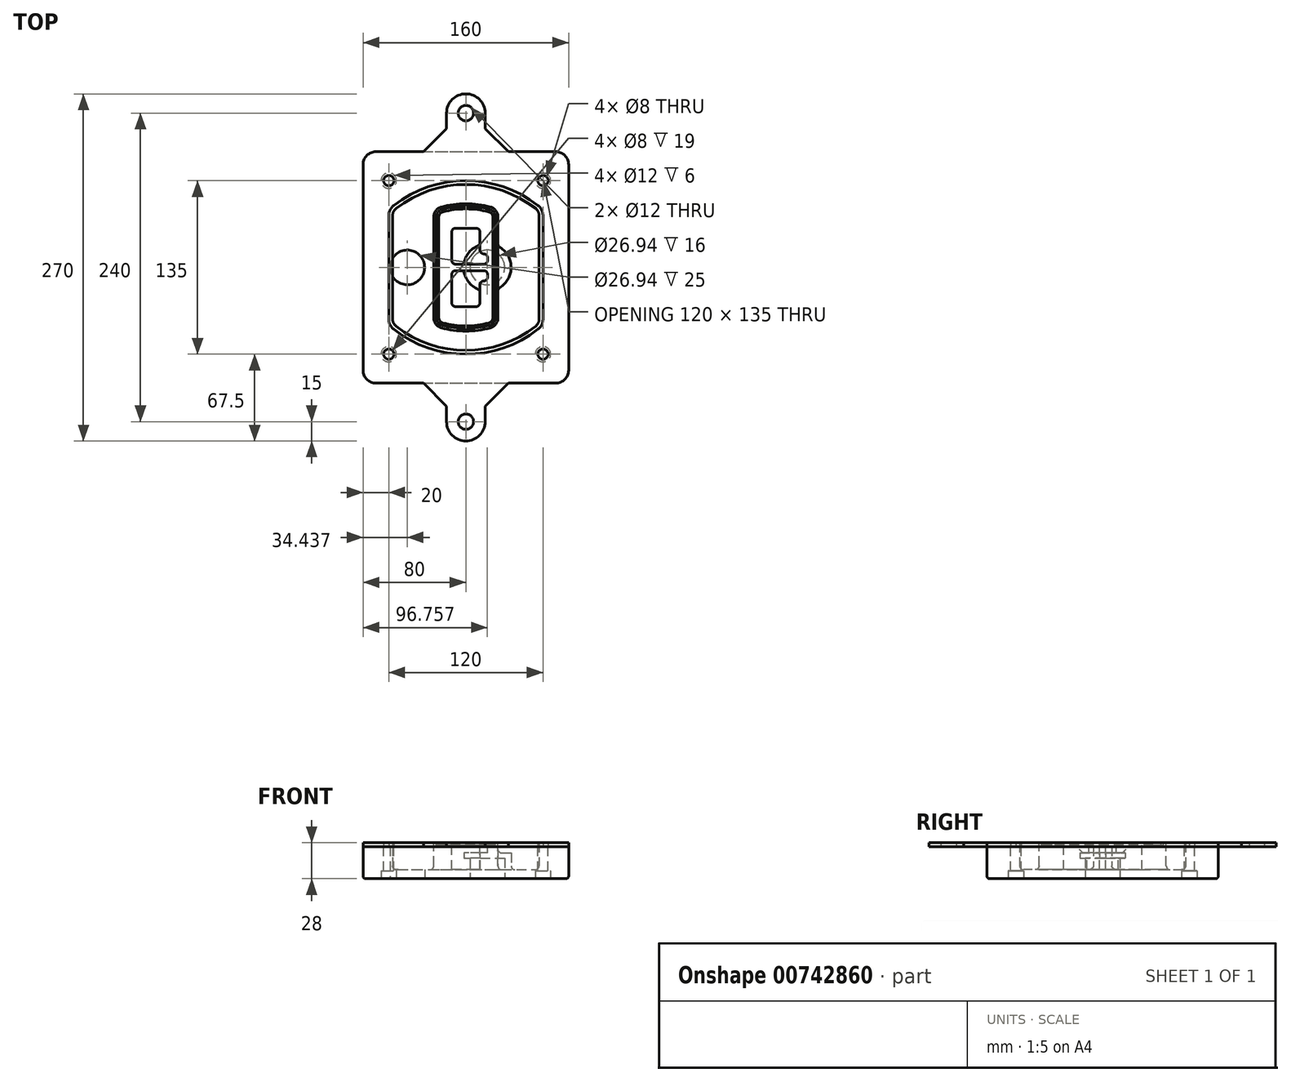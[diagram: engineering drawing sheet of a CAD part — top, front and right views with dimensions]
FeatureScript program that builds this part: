
annotation { "Feature Type Name" : "Feature", "Feature Type Description" : "" }
export const myFeature = defineFeature(function(context is Context, id is Id, definition is map)
    precondition{}
    {
        {
            var Q0;
            Q0=qCreatedBy(makeId("Top.planeOp"),FACE);
            var sketch = newSketch(context, id + "F0", { "sketchPlane" : qUnion([Q0])});
            skPoint(sketch, "E0.rect.middle", {"position": v(0, 0) * mm});
            skLineSegment(sketch, "E1.bottom", {"start": v(-70, -90) * mm, "end": v(70, -90) * mm});
            skLineSegment(sketch, "E1.top", {"start": v(-70, 90) * mm, "end": v(70, 90) * mm});
            skLineSegment(sketch, "E1.left", {"start": v(-80, -80) * mm, "end": v(-80, 80) * mm});
            skLineSegment(sketch, "E1.right", {"start": v(80, -80) * mm, "end": v(80, 80) * mm});
            skLineSegment(sketch, "E2", {"start": v(-80, 90) * mm, "end": v(80, -90) * mm, "construction": true});
            skLineSegment(sketch, "E3", {"start": v(80, 90) * mm, "end": v(-80, -90) * mm, "construction": true});
            skCircle(sketch, "E4", {"center": v(-60, 67.5) * mm, "radius": 4 * mm});
            skCircle(sketch, "E5", {"center": v(60, 67.5) * mm, "radius": 4 * mm});
            skCircle(sketch, "E6", {"center": v(60, -67.5) * mm, "radius": 4 * mm});
            skCircle(sketch, "E7", {"center": v(-60, -67.5) * mm, "radius": 4 * mm});
            skLineSegment(sketch, "E8", {"start": v(-60, 67.5) * mm, "end": v(60, 67.5) * mm, "construction": true});
            skLineSegment(sketch, "E9", {"start": v(60, 67.5) * mm, "end": v(60, -67.5) * mm, "construction": true});
            skLineSegment(sketch, "E10", {"start": v(60, -67.5) * mm, "end": v(-60, -67.5) * mm, "construction": true});
            skLineSegment(sketch, "E11", {"start": v(-60, -67.5) * mm, "end": v(-60, 67.5) * mm, "construction": true});
            skLineSegment(sketch, "E12", {"start": v(-60, 40.3) * mm, "end": v(-60, -40.3) * mm});
            skLineSegment(sketch, "E13", {"start": v(60, 40.3) * mm, "end": v(60, -40.3) * mm});
            skArc(sketch, "E14", {"start": v(56.15, 48.18) * mm, "mid": v(0, 67.5) * mm, "end": v(-56.15, 48.18) * mm});
            skArc(sketch, "E15", {"start": v(-56.15, -48.18) * mm, "mid": v(0, -67.5) * mm, "end": v(56.15, -48.18) * mm});
            skLineSegment(sketch, "E16", {"start": v(-60, 0) * mm, "end": v(60, 0) * mm, "construction": true});
            skPoint(sketch, "E17.visualSharp", {"position": v(-60, -45) * mm});
            skArc(sketch, "E17.filletArc", {"start": v(-60, -40.3) * mm, "mid": v(-58.99, -44.68) * mm, "end": v(-56.15, -48.18) * mm});
            skPoint(sketch, "E18.visualSharp", {"position": v(-60, 45) * mm});
            skArc(sketch, "E18.filletArc", {"start": v(-56.15, 48.18) * mm, "mid": v(-58.99, 44.68) * mm, "end": v(-60, 40.3) * mm});
            skPoint(sketch, "E19.visualSharp", {"position": v(60, 45) * mm});
            skArc(sketch, "E19.filletArc", {"start": v(60, 40.3) * mm, "mid": v(58.99, 44.68) * mm, "end": v(56.15, 48.18) * mm});
            skPoint(sketch, "E20.visualSharp", {"position": v(60, -45) * mm});
            skArc(sketch, "E20.filletArc", {"start": v(56.15, -48.18) * mm, "mid": v(58.99, -44.68) * mm, "end": v(60, -40.3) * mm});
            skPoint(sketch, "E21.visualSharp", {"position": v(-80, 90) * mm});
            skArc(sketch, "E21.filletArc", {"start": v(-70, 90) * mm, "mid": v(-77.07, 87.07) * mm, "end": v(-80, 80) * mm});
            skPoint(sketch, "E22.visualSharp", {"position": v(80, 90) * mm});
            skArc(sketch, "E22.filletArc", {"start": v(80, 80) * mm, "mid": v(77.07, 87.07) * mm, "end": v(70, 90) * mm});
            skPoint(sketch, "E23.visualSharp", {"position": v(80, -90) * mm});
            skArc(sketch, "E23.filletArc", {"start": v(70, -90) * mm, "mid": v(77.07, -87.07) * mm, "end": v(80, -80) * mm});
            skPoint(sketch, "E24.visualSharp", {"position": v(-80, -90) * mm});
            skArc(sketch, "E24.filletArc", {"start": v(-80, -80) * mm, "mid": v(-77.07, -87.07) * mm, "end": v(-70, -90) * mm});
            skArc(sketch, "E25.0", {"start": v(57, 40.3) * mm, "mid": v(56.3, 43.36) * mm, "end": v(54.3, 45.81) * mm});
            skLineSegment(sketch, "E25.1", {"start": v(57, 40.3) * mm, "end": v(57, -40.3) * mm});
            skArc(sketch, "E25.2", {"start": v(54.3, -45.81) * mm, "mid": v(56.3, -43.36) * mm, "end": v(57, -40.3) * mm});
            skArc(sketch, "E25.3", {"start": v(-54.3, -45.81) * mm, "mid": v(0, -64.5) * mm, "end": v(54.3, -45.81) * mm});
            skArc(sketch, "E25.4", {"start": v(-57, -40.3) * mm, "mid": v(-56.3, -43.36) * mm, "end": v(-54.3, -45.81) * mm});
            skArc(sketch, "E25.5", {"start": v(54.3, 45.81) * mm, "mid": v(0, 64.5) * mm, "end": v(-54.3, 45.81) * mm});
            skLineSegment(sketch, "E25.6", {"start": v(-57, 40.3) * mm, "end": v(-57, -40.3) * mm});
            skArc(sketch, "E25.7", {"start": v(-54.3, 45.81) * mm, "mid": v(-56.3, 43.36) * mm, "end": v(-57, 40.3) * mm});
            skArc(sketch, "E26.0", {"start": v(-58.62, 51.33) * mm, "mid": v(-62.58, 46.43) * mm, "end": v(-64, 40.3) * mm});
            skArc(sketch, "E26.1", {"start": v(58.62, 51.33) * mm, "mid": v(0, 71.5) * mm, "end": v(-58.62, 51.33) * mm});
            skArc(sketch, "E26.2", {"start": v(64, 40.3) * mm, "mid": v(62.58, 46.43) * mm, "end": v(58.62, 51.33) * mm});
            skLineSegment(sketch, "E26.3", {"start": v(64, 40.3) * mm, "end": v(64, -40.3) * mm});
            skArc(sketch, "E26.4", {"start": v(58.62, -51.33) * mm, "mid": v(62.58, -46.43) * mm, "end": v(64, -40.3) * mm});
            skLineSegment(sketch, "E26.5", {"start": v(-64, 40.3) * mm, "end": v(-64, -40.3) * mm});
            skArc(sketch, "E26.6", {"start": v(-58.62, -51.33) * mm, "mid": v(0, -71.5) * mm, "end": v(58.62, -51.33) * mm});
            skArc(sketch, "E26.7", {"start": v(-64, -40.3) * mm, "mid": v(-62.58, -46.43) * mm, "end": v(-58.62, -51.33) * mm});
            skSolve(sketch);
        }
        {
            var Q0;
            Q0=makeQuery(id+"F0.imprint","IMPRINT",FACE,{"disambiguationData":[TD([[makeQuery(id+"F0.imprint","IMPRINT",EDGE,{"derivedFrom":sQuery(id+"F0.wireOp",EDGE,"E1.bottom")}),1.0]])]});
            var Q1;
            Q1=makeQuery(id+"F0.imprint","IMPRINT",FACE,{"disambiguationData":[TD([[makeQuery(id+"F0.imprint","IMPRINT",EDGE,{"derivedFrom":sQuery(id+"F0.wireOp",EDGE,"E12")}),1.0]])]});
            var Q2;
            Q2=makeQuery(id+"F0.imprint","IMPRINT",FACE,{"disambiguationData":[TD([[makeQuery(id+"F0.imprint","IMPRINT",EDGE,{"derivedFrom":sQuery(id+"F0.wireOp",EDGE,"E25.0")}),1.0]])]});
            var Q3;
            Q3=makeQuery(id+"F0.imprint","IMPRINT",FACE,{"disambiguationData":[TD([[makeQuery(id+"F0.imprint","IMPRINT",EDGE,{"derivedFrom":sQuery(id+"F0.wireOp",EDGE,"E12")}),-1.0]])]});
            extrude(context, id + "F1", {"entities" : qUnion([Q0, Q1, Q2, Q3]), "oppositeDirection" : true, "depth" : 25 * mm});
        }
        {
            var Q0;
            Q0=makeQuery(id+"F0.imprint","IMPRINT",FACE,{"disambiguationData":[TD([[makeQuery(id+"F0.imprint","IMPRINT",EDGE,{"derivedFrom":sQuery(id+"F0.wireOp",EDGE,"E12")}),1.0]])]});
            extrude(context, id + "F2", {"entities" : qUnion([Q0]), "operationType" : NewBodyOperationType.ADD, "depth" : 3 * mm});
        }
        {
            var Q0;
            Q0=makeQuery(id+"F0.imprint","IMPRINT",FACE,{"disambiguationData":[TD([[makeQuery(id+"F0.imprint","IMPRINT",EDGE,{"derivedFrom":sQuery(id+"F0.wireOp",EDGE,"E25.0")}),1.0]])]});
            extrude(context, id + "F3", {"entities" : qUnion([Q0]), "operationType" : NewBodyOperationType.REMOVE, "oppositeDirection" : true, "depth" : 18 * mm});
        }
        {
            var Q0;
            Q0=makeQuery(id+"F2.opExtrude","CAP_FACE",FACE,{"disambiguationData":[OSD([sQuery(id+"F0.wireOp",EDGE,"E12"),sQuery(id+"F0.wireOp",EDGE,"E13"),sQuery(id+"F0.wireOp",EDGE,"E14"),sQuery(id+"F0.wireOp",EDGE,"E15"),sQuery(id+"F0.wireOp",EDGE,"E17.filletArc"),sQuery(id+"F0.wireOp",EDGE,"E18.filletArc"),sQuery(id+"F0.wireOp",EDGE,"E19.filletArc"),sQuery(id+"F0.wireOp",EDGE,"E20.filletArc"),sQuery(id+"F0.wireOp",EDGE,"E25.0"),sQuery(id+"F0.wireOp",EDGE,"E25.1"),sQuery(id+"F0.wireOp",EDGE,"E25.2"),sQuery(id+"F0.wireOp",EDGE,"E25.3"),sQuery(id+"F0.wireOp",EDGE,"E25.4"),sQuery(id+"F0.wireOp",EDGE,"E25.5"),sQuery(id+"F0.wireOp",EDGE,"E25.6"),sQuery(id+"F0.wireOp",EDGE,"E25.7")])],"isStart":false});
            var sketch = newSketch(context, id + "F4", { "sketchPlane" : qUnion([Q0])});
            skArc(sketch, "E27.0", {"start": v(-19.08, -46.97) * mm, "mid": v(0, -49.5) * mm, "end": v(19.08, -46.97) * mm});
            skArc(sketch, "E28.0", {"start": v(19.08, 46.97) * mm, "mid": v(0, 49.5) * mm, "end": v(-19.08, 46.97) * mm});
            skLineSegment(sketch, "E29", {"start": v(-25, 39.25) * mm, "end": v(-25, -39.25) * mm});
            skLineSegment(sketch, "E30", {"start": v(25, 39.25) * mm, "end": v(25, -39.25) * mm});
            skLineSegment(sketch, "E31", {"start": v(-25, 45.1) * mm, "end": v(25, 45.1) * mm, "construction": true});
            skLineSegment(sketch, "E32", {"start": v(-25, -45.1) * mm, "end": v(25, -45.1) * mm, "construction": true});
            skPoint(sketch, "E33.visualSharp", {"position": v(-25, 45.1) * mm});
            skArc(sketch, "E33.filletArc", {"start": v(-19.08, 46.97) * mm, "mid": v(-23.35, 44.11) * mm, "end": v(-25, 39.25) * mm});
            skPoint(sketch, "E34.visualSharp", {"position": v(25, 45.1) * mm});
            skArc(sketch, "E34.filletArc", {"start": v(25, 39.25) * mm, "mid": v(23.35, 44.11) * mm, "end": v(19.08, 46.97) * mm});
            skPoint(sketch, "E35.visualSharp", {"position": v(25, -45.1) * mm});
            skArc(sketch, "E35.filletArc", {"start": v(19.08, -46.97) * mm, "mid": v(23.35, -44.11) * mm, "end": v(25, -39.25) * mm});
            skPoint(sketch, "E36.visualSharp", {"position": v(-25, -45.1) * mm});
            skArc(sketch, "E36.filletArc", {"start": v(-25, -39.25) * mm, "mid": v(-23.35, -44.11) * mm, "end": v(-19.08, -46.97) * mm});
            skArc(sketch, "E37.0", {"start": v(54.3, 45.81) * mm, "mid": v(0, 64.5) * mm, "end": v(-54.3, 45.81) * mm});
            skArc(sketch, "E37.1", {"start": v(-54.3, 45.81) * mm, "mid": v(-56.3, 43.36) * mm, "end": v(-57, 40.3) * mm});
            skLineSegment(sketch, "E37.2", {"start": v(-57, 40.3) * mm, "end": v(-57, -40.3) * mm});
            skArc(sketch, "E37.3", {"start": v(-57, -40.3) * mm, "mid": v(-56.3, -43.36) * mm, "end": v(-54.3, -45.81) * mm});
            skArc(sketch, "E37.4", {"start": v(-54.3, -45.81) * mm, "mid": v(0, -64.5) * mm, "end": v(54.3, -45.81) * mm});
            skArc(sketch, "E37.5", {"start": v(54.3, -45.81) * mm, "mid": v(56.3, -43.36) * mm, "end": v(57, -40.3) * mm});
            skLineSegment(sketch, "E37.6", {"start": v(57, 40.3) * mm, "end": v(57, -40.3) * mm});
            skArc(sketch, "E37.7", {"start": v(57, 40.3) * mm, "mid": v(56.3, 43.36) * mm, "end": v(54.3, 45.81) * mm});
            skLineSegment(sketch, "E38.0", {"start": v(23, 39.25) * mm, "end": v(23, -39.25) * mm});
            skArc(sketch, "E38.1", {"start": v(18.56, -45.04) * mm, "mid": v(21.76, -42.9) * mm, "end": v(23, -39.25) * mm});
            skArc(sketch, "E38.2", {"start": v(-18.56, -45.04) * mm, "mid": v(0, -47.5) * mm, "end": v(18.56, -45.04) * mm});
            skArc(sketch, "E38.3", {"start": v(-23, -39.25) * mm, "mid": v(-21.76, -42.9) * mm, "end": v(-18.56, -45.04) * mm});
            skLineSegment(sketch, "E38.4", {"start": v(-23, 39.25) * mm, "end": v(-23, -39.25) * mm});
            skArc(sketch, "E38.5", {"start": v(23, 39.25) * mm, "mid": v(21.76, 42.9) * mm, "end": v(18.56, 45.04) * mm});
            skArc(sketch, "E38.6", {"start": v(-18.56, 45.04) * mm, "mid": v(-21.76, 42.9) * mm, "end": v(-23, 39.25) * mm});
            skArc(sketch, "E38.7", {"start": v(18.56, 45.04) * mm, "mid": v(0, 47.5) * mm, "end": v(-18.56, 45.04) * mm});
            skArc(sketch, "E39.0", {"start": v(21, 39.25) * mm, "mid": v(20.18, 41.68) * mm, "end": v(18.04, 43.1) * mm});
            skLineSegment(sketch, "E39.1", {"start": v(21, 39.25) * mm, "end": v(21, -39.25) * mm});
            skArc(sketch, "E39.2", {"start": v(18.04, -43.1) * mm, "mid": v(20.18, -41.68) * mm, "end": v(21, -39.25) * mm});
            skArc(sketch, "E39.3", {"start": v(-18.04, -43.1) * mm, "mid": v(0, -45.5) * mm, "end": v(18.04, -43.1) * mm});
            skArc(sketch, "E39.4", {"start": v(-21, -39.25) * mm, "mid": v(-20.18, -41.68) * mm, "end": v(-18.04, -43.1) * mm});
            skArc(sketch, "E39.5", {"start": v(18.04, 43.1) * mm, "mid": v(0, 45.5) * mm, "end": v(-18.04, 43.1) * mm});
            skLineSegment(sketch, "E39.6", {"start": v(-21, 39.25) * mm, "end": v(-21, -39.25) * mm});
            skArc(sketch, "E39.7", {"start": v(-18.04, 43.1) * mm, "mid": v(-20.18, 41.68) * mm, "end": v(-21, 39.25) * mm});
            skLineSegment(sketch, "E40", {"start": v(-25, 0) * mm, "end": v(25, 0) * mm, "construction": true});
            skLineSegment(sketch, "E41", {"start": v(-11, 5.5) * mm, "end": v(-11, 27.5) * mm});
            skLineSegment(sketch, "E42", {"start": v(-8, 30.5) * mm, "end": v(8, 30.5) * mm});
            skLineSegment(sketch, "E43", {"start": v(11, 27.5) * mm, "end": v(11, 13.5) * mm});
            skLineSegment(sketch, "E44", {"start": v(14, 10.5) * mm, "end": v(14, 10.5) * mm});
            skLineSegment(sketch, "E45", {"start": v(17, 7.5) * mm, "end": v(17, 5.5) * mm});
            skLineSegment(sketch, "E46", {"start": v(14, 2.5) * mm, "end": v(-8, 2.5) * mm});
            skPoint(sketch, "E47.visualSharp", {"position": v(-11, 30.5) * mm});
            skArc(sketch, "E47.filletArc", {"start": v(-8, 30.5) * mm, "mid": v(-10.12, 29.62) * mm, "end": v(-11, 27.5) * mm});
            skPoint(sketch, "E48.visualSharp", {"position": v(11, 30.5) * mm});
            skArc(sketch, "E48.filletArc", {"start": v(11, 27.5) * mm, "mid": v(10.12, 29.62) * mm, "end": v(8, 30.5) * mm});
            skPoint(sketch, "E49.visualSharp", {"position": v(11, 10.5) * mm});
            skArc(sketch, "E49.filletArc", {"start": v(11, 13.5) * mm, "mid": v(11.88, 11.38) * mm, "end": v(14, 10.5) * mm});
            skPoint(sketch, "E50.visualSharp", {"position": v(17, 10.5) * mm});
            skArc(sketch, "E50.filletArc", {"start": v(17, 7.5) * mm, "mid": v(16.12, 9.62) * mm, "end": v(14, 10.5) * mm});
            skPoint(sketch, "E51.visualSharp", {"position": v(17, 2.5) * mm});
            skArc(sketch, "E51.filletArc", {"start": v(14, 2.5) * mm, "mid": v(16.12, 3.38) * mm, "end": v(17, 5.5) * mm});
            skPoint(sketch, "E52.visualSharp", {"position": v(-11, 2.5) * mm});
            skArc(sketch, "E52.filletArc", {"start": v(-11, 5.5) * mm, "mid": v(-10.12, 3.38) * mm, "end": v(-8, 2.5) * mm});
            skLineSegment(sketch, "E53.0.MirrorCS", {"start": v(14, -2.5) * mm, "end": v(-8, -2.5) * mm});
            skArc(sketch, "E54.0.MirrorCS", {"start": v(-11, -5.5) * mm, "mid": v(-10.12, -3.38) * mm, "end": v(-8, -2.5) * mm});
            skLineSegment(sketch, "E55.0.MirrorCS", {"start": v(-11, -5.5) * mm, "end": v(-11, -27.5) * mm});
            skArc(sketch, "E56.0.MirrorCS", {"start": v(-8, -30.5) * mm, "mid": v(-10.12, -29.62) * mm, "end": v(-11, -27.5) * mm});
            skLineSegment(sketch, "E57.0.MirrorCS", {"start": v(-8, -30.5) * mm, "end": v(8, -30.5) * mm});
            skArc(sketch, "E58.0.MirrorCS", {"start": v(11, -27.5) * mm, "mid": v(10.12, -29.62) * mm, "end": v(8, -30.5) * mm});
            skLineSegment(sketch, "E59.0.MirrorCS", {"start": v(11, -27.5) * mm, "end": v(11, -13.5) * mm});
            skArc(sketch, "E60.0.MirrorCS", {"start": v(11, -13.5) * mm, "mid": v(11.88, -11.38) * mm, "end": v(14, -10.5) * mm});
            skArc(sketch, "E61.0.MirrorCS", {"start": v(17, -7.5) * mm, "mid": v(16.12, -9.62) * mm, "end": v(14, -10.5) * mm});
            skLineSegment(sketch, "E62.0.MirrorCS", {"start": v(17, -7.5) * mm, "end": v(17, -5.5) * mm});
            skArc(sketch, "E63.0.MirrorCS", {"start": v(14, -2.5) * mm, "mid": v(16.12, -3.38) * mm, "end": v(17, -5.5) * mm});
            skSolve(sketch);
        }
        {
            var Q0;
            Q0=makeQuery(id+"F4.imprint","IMPRINT",FACE,{"disambiguationData":[TD([[makeQuery(id+"F4.imprint","IMPRINT",EDGE,{"derivedFrom":sQuery(id+"F4.wireOp",EDGE,"E27.0")}),1.0]])]});
            var Q1;
            Q1=makeQuery(id+"F4.imprint","IMPRINT",FACE,{"disambiguationData":[TD([[makeQuery(id+"F4.imprint","IMPRINT",EDGE,{"derivedFrom":sQuery(id+"F4.wireOp",EDGE,"E38.0")}),-1.0]])]});
            var Q2;
            Q2=makeQuery(id+"F4.imprint","IMPRINT",FACE,{"disambiguationData":[TD([[makeQuery(id+"F4.imprint","IMPRINT",EDGE,{"derivedFrom":sQuery(id+"F4.wireOp",EDGE,"E39.0")}),1.0]])]});
            extrude(context, id + "F5", {"entities" : qUnion([Q0, Q1, Q2]), "operationType" : NewBodyOperationType.ADD, "endBound" : BoundingType.UP_TO_NEXT, "oppositeDirection" : true, "depth" : 25 * mm});
        }
        {
            var Q0;
            Q0=makeQuery(id+"F4.imprint","IMPRINT",FACE,{"disambiguationData":[TD([[makeQuery(id+"F4.imprint","IMPRINT",EDGE,{"derivedFrom":sQuery(id+"F4.wireOp",EDGE,"E38.0")}),-1.0]])]});
            extrude(context, id + "F6", {"entities" : qUnion([Q0]), "operationType" : NewBodyOperationType.REMOVE, "oppositeDirection" : true, "depth" : 2 * mm});
        }
        {
            var Q0;
            Q0=makeQuery(id+"F1.opExtrude","CAP_FACE",FACE,{"disambiguationData":[OSD([sQuery(id+"F0.wireOp",EDGE,"E1.bottom"),sQuery(id+"F0.wireOp",EDGE,"E1.top"),sQuery(id+"F0.wireOp",EDGE,"E1.left"),sQuery(id+"F0.wireOp",EDGE,"E1.right"),sQuery(id+"F0.wireOp",EDGE,"E4"),sQuery(id+"F0.wireOp",EDGE,"E5"),sQuery(id+"F0.wireOp",EDGE,"E6"),sQuery(id+"F0.wireOp",EDGE,"E7"),sQuery(id+"F0.wireOp",EDGE,"E21.filletArc"),sQuery(id+"F0.wireOp",EDGE,"E22.filletArc"),sQuery(id+"F0.wireOp",EDGE,"E23.filletArc"),sQuery(id+"F0.wireOp",EDGE,"E24.filletArc")])],"isStart":false});
            var sketch = newSketch(context, id + "F7", { "sketchPlane" : qUnion([Q0])});
            skCircle(sketch, "E64", {"center": v(16.76, 0) * mm, "radius": 13.47 * mm});
            skCircle(sketch, "E65", {"center": v(-45.56, 0) * mm, "radius": 13.47 * mm});
            skLineSegment(sketch, "E66", {"start": v(80, 0) * mm, "end": v(-80, 0) * mm});
            skCircle(sketch, "E67", {"center": v(16.76, 0) * mm, "radius": 18.47 * mm});
            skCircle(sketch, "E68", {"center": v(60, -67.5) * mm, "radius": 6 * mm});
            skCircle(sketch, "E69", {"center": v(-60, -67.5) * mm, "radius": 6 * mm});
            skCircle(sketch, "E70", {"center": v(-60, 67.5) * mm, "radius": 6 * mm});
            skCircle(sketch, "E71", {"center": v(60, 67.5) * mm, "radius": 6 * mm});
            skSolve(sketch);
        }
        {
            var Q0;
            {var subQ1=sQuery(id+"F7.wireOp",EDGE,"E66");var subQ4=sQuery(id+"F7.wireOp",EDGE,"E64");var subQ6=makeQuery(id+"F7.imprint","INTERSECT",VERTEX,{"disambiguationData":[OD(0.0)],"derivedFrom":[subQ4,subQ1]});Q0=makeQuery(id+"F7.imprint","IMPRINT",FACE,{"disambiguationData":[TD([[makeQuery(id+"F7.imprint","IMPRINT",EDGE,{"disambiguationData":[TD([[subQ6,-1.0]])],"derivedFrom":subQ4}),-1.0]])]});}
            var Q1;
            {var subQ0=sQuery(id+"F7.wireOp",EDGE,"E66");var subQ1=sQuery(id+"F7.wireOp",EDGE,"E64");var subQ3=makeQuery(id+"F7.imprint","INTERSECT",VERTEX,{"disambiguationData":[OD(0.0)],"derivedFrom":[subQ1,subQ0]});Q1=makeQuery(id+"F7.imprint","IMPRINT",FACE,{"disambiguationData":[TD([[makeQuery(id+"F7.imprint","IMPRINT",EDGE,{"disambiguationData":[TD([[subQ3,-1.0]])],"derivedFrom":subQ1}),1.0]])]});}
            var Q2;
            {var subQ0=sQuery(id+"F7.wireOp",EDGE,"E66");var subQ1=sQuery(id+"F7.wireOp",EDGE,"E64");var subQ3=makeQuery(id+"F7.imprint","INTERSECT",VERTEX,{"disambiguationData":[OD(0.0)],"derivedFrom":[subQ1,subQ0]});Q2=makeQuery(id+"F7.imprint","IMPRINT",FACE,{"disambiguationData":[TD([[makeQuery(id+"F7.imprint","IMPRINT",EDGE,{"disambiguationData":[TD([[subQ3,1.0]])],"derivedFrom":subQ1}),1.0]])]});}
            var Q3;
            {var subQ1=sQuery(id+"F7.wireOp",EDGE,"E66");var subQ4=sQuery(id+"F7.wireOp",EDGE,"E64");var subQ6=makeQuery(id+"F7.imprint","INTERSECT",VERTEX,{"disambiguationData":[OD(0.0)],"derivedFrom":[subQ4,subQ1]});Q3=makeQuery(id+"F7.imprint","IMPRINT",FACE,{"disambiguationData":[TD([[makeQuery(id+"F7.imprint","IMPRINT",EDGE,{"disambiguationData":[TD([[subQ6,1.0]])],"derivedFrom":subQ4}),-1.0]])]});}
            extrude(context, id + "F8", {"entities" : qUnion([Q0, Q1, Q2, Q3]), "operationType" : NewBodyOperationType.ADD, "oppositeDirection" : true, "depth" : 20 * mm});
        }
        {
            var Q0;
            {var subQ0=sQuery(id+"F7.wireOp",EDGE,"E66");var subQ1=sQuery(id+"F7.wireOp",EDGE,"E64");var subQ3=makeQuery(id+"F7.imprint","INTERSECT",VERTEX,{"disambiguationData":[OD(0.0)],"derivedFrom":[subQ1,subQ0]});Q0=makeQuery(id+"F7.imprint","IMPRINT",FACE,{"disambiguationData":[TD([[makeQuery(id+"F7.imprint","IMPRINT",EDGE,{"disambiguationData":[TD([[subQ3,-1.0]])],"derivedFrom":subQ1}),1.0]])]});}
            var Q1;
            {var subQ0=sQuery(id+"F7.wireOp",EDGE,"E66");var subQ1=sQuery(id+"F7.wireOp",EDGE,"E64");var subQ3=makeQuery(id+"F7.imprint","INTERSECT",VERTEX,{"disambiguationData":[OD(0.0)],"derivedFrom":[subQ1,subQ0]});Q1=makeQuery(id+"F7.imprint","IMPRINT",FACE,{"disambiguationData":[TD([[makeQuery(id+"F7.imprint","IMPRINT",EDGE,{"disambiguationData":[TD([[subQ3,1.0]])],"derivedFrom":subQ1}),1.0]])]});}
            extrude(context, id + "F9", {"entities" : qUnion([Q0, Q1]), "operationType" : NewBodyOperationType.REMOVE, "oppositeDirection" : true, "depth" : 16 * mm});
        }
        {
            var Q0;
            {var subQ0=sQuery(id+"F7.wireOp",EDGE,"E66");var subQ1=sQuery(id+"F7.wireOp",EDGE,"E65");var subQ3=makeQuery(id+"F7.imprint","INTERSECT",VERTEX,{"disambiguationData":[OD(0.0)],"derivedFrom":[subQ1,subQ0]});Q0=makeQuery(id+"F7.imprint","IMPRINT",FACE,{"disambiguationData":[TD([[makeQuery(id+"F7.imprint","IMPRINT",EDGE,{"disambiguationData":[TD([[subQ3,-1.0]])],"derivedFrom":subQ1}),1.0]])]});}
            var Q1;
            {var subQ0=sQuery(id+"F7.wireOp",EDGE,"E66");var subQ1=sQuery(id+"F7.wireOp",EDGE,"E65");var subQ3=makeQuery(id+"F7.imprint","INTERSECT",VERTEX,{"disambiguationData":[OD(0.0)],"derivedFrom":[subQ1,subQ0]});Q1=makeQuery(id+"F7.imprint","IMPRINT",FACE,{"disambiguationData":[TD([[makeQuery(id+"F7.imprint","IMPRINT",EDGE,{"disambiguationData":[TD([[subQ3,1.0]])],"derivedFrom":subQ1}),1.0]])]});}
            extrude(context, id + "F10", {"entities" : qUnion([Q0, Q1]), "operationType" : NewBodyOperationType.REMOVE, "oppositeDirection" : true, "depth" : 25 * mm});
        }
        {
            var Q0;
            Q0=makeQuery(id+"F7.imprint","IMPRINT",FACE,{"disambiguationData":[TD([[makeQuery(id+"F7.imprint","IMPRINT",EDGE,{"derivedFrom":sQuery(id+"F7.wireOp",EDGE,"E68")}),1.0]])]});
            var Q1;
            Q1=makeQuery(id+"F7.imprint","IMPRINT",FACE,{"disambiguationData":[TD([[makeQuery(id+"F7.imprint","IMPRINT",EDGE,{"derivedFrom":makeQuery(id+"F1.opExtrude","CAP_EDGE",EDGE,{"disambiguationData":[OSD([sQuery(id+"F0.wireOp",EDGE,"E5")])],"isStart":false})}),-1.0]])]});
            var Q2;
            Q2=makeQuery(id+"F7.imprint","IMPRINT",FACE,{"disambiguationData":[TD([[makeQuery(id+"F7.imprint","IMPRINT",EDGE,{"derivedFrom":sQuery(id+"F7.wireOp",EDGE,"E69")}),1.0]])]});
            var Q3;
            Q3=makeQuery(id+"F7.imprint","IMPRINT",FACE,{"disambiguationData":[TD([[makeQuery(id+"F7.imprint","IMPRINT",EDGE,{"derivedFrom":makeQuery(id+"F1.opExtrude","CAP_EDGE",EDGE,{"disambiguationData":[OSD([sQuery(id+"F0.wireOp",EDGE,"E4")])],"isStart":false})}),-1.0]])]});
            var Q4;
            Q4=makeQuery(id+"F7.imprint","IMPRINT",FACE,{"disambiguationData":[TD([[makeQuery(id+"F7.imprint","IMPRINT",EDGE,{"derivedFrom":sQuery(id+"F7.wireOp",EDGE,"E70")}),1.0]])]});
            var Q5;
            Q5=makeQuery(id+"F7.imprint","IMPRINT",FACE,{"disambiguationData":[TD([[makeQuery(id+"F7.imprint","IMPRINT",EDGE,{"derivedFrom":makeQuery(id+"F1.opExtrude","CAP_EDGE",EDGE,{"disambiguationData":[OSD([sQuery(id+"F0.wireOp",EDGE,"E7")])],"isStart":false})}),-1.0]])]});
            var Q6;
            Q6=makeQuery(id+"F7.imprint","IMPRINT",FACE,{"disambiguationData":[TD([[makeQuery(id+"F7.imprint","IMPRINT",EDGE,{"derivedFrom":sQuery(id+"F7.wireOp",EDGE,"E71")}),1.0]])]});
            var Q7;
            Q7=makeQuery(id+"F7.imprint","IMPRINT",FACE,{"disambiguationData":[TD([[makeQuery(id+"F7.imprint","IMPRINT",EDGE,{"derivedFrom":makeQuery(id+"F1.opExtrude","CAP_EDGE",EDGE,{"disambiguationData":[OSD([sQuery(id+"F0.wireOp",EDGE,"E6")])],"isStart":false})}),-1.0]])]});
            extrude(context, id + "F11", {"entities" : qUnion([Q0, Q1, Q2, Q3, Q4, Q5, Q6, Q7]), "operationType" : NewBodyOperationType.REMOVE, "oppositeDirection" : true, "depth" : 6 * mm});
        }
        {
            var Q0;
            Q0=makeQuery(id+"F9.boolean.opBoolean","COPY",FACE,{"derivedFrom":makeQuery(id+"F9.opExtrude","CAP_FACE",FACE,{"disambiguationData":[OSD([sQuery(id+"F7.wireOp",EDGE,"E64")])],"isStart":false})});
            var sketch = newSketch(context, id + "F12", { "sketchPlane" : qUnion([Q0])});
            skArc(sketch, "E72.0", {"start": v(11, 17.55) * mm, "mid": v(2.57, 11.82) * mm, "end": v(-1.54, 2.5) * mm});
            skArc(sketch, "E72.1", {"start": v(-1.54, -2.5) * mm, "mid": v(2.57, -11.82) * mm, "end": v(11, -17.55) * mm});
            skLineSegment(sketch, "E73", {"start": v(-1.54, -2.5) * mm, "end": v(14, -2.5) * mm});
            skLineSegment(sketch, "E74.0", {"start": v(14, 2.5) * mm, "end": v(-1.54, 2.5) * mm});
            skArc(sketch, "E74.1", {"start": v(14, 2.5) * mm, "mid": v(16.12, 3.38) * mm, "end": v(17, 5.5) * mm});
            skLineSegment(sketch, "E74.2", {"start": v(17, 7.5) * mm, "end": v(17, 5.5) * mm});
            skArc(sketch, "E74.3", {"start": v(17, 7.5) * mm, "mid": v(16.12, 9.62) * mm, "end": v(14, 10.5) * mm});
            skArc(sketch, "E74.4", {"start": v(11, 13.5) * mm, "mid": v(11.88, 11.38) * mm, "end": v(14, 10.5) * mm});
            skLineSegment(sketch, "E74.5", {"start": v(11, 17.55) * mm, "end": v(11, 13.5) * mm});
            skLineSegment(sketch, "E74.7", {"start": v(14, -2.5) * mm, "end": v(-1.54, -2.5) * mm});
            skArc(sketch, "E74.8", {"start": v(14, -2.5) * mm, "mid": v(16.12, -3.38) * mm, "end": v(17, -5.5) * mm});
            skLineSegment(sketch, "E74.9", {"start": v(17, -7.5) * mm, "end": v(17, -5.5) * mm});
            skArc(sketch, "E74.10", {"start": v(17, -7.5) * mm, "mid": v(16.12, -9.62) * mm, "end": v(14, -10.5) * mm});
            skArc(sketch, "E74.11", {"start": v(11, -13.5) * mm, "mid": v(11.88, -11.38) * mm, "end": v(14, -10.5) * mm});
            skLineSegment(sketch, "E74.12", {"start": v(11, -17.55) * mm, "end": v(11, -13.5) * mm});
            skPoint(sketch, "E75.orphan", {"position": v(11, -27.5) * mm});
            skPoint(sketch, "E76.orphan", {"position": v(-8, -2.5) * mm});
            skPoint(sketch, "E77.orphan", {"position": v(-8, 2.5) * mm});
            skPoint(sketch, "E78.orphan", {"position": v(11, 27.5) * mm});
            skSolve(sketch);
        }
        {
            var Q0;
            {var subQ7=sQuery(id+"F12.wireOp",EDGE,"E72.0");var subQ14=sQuery(id+"F12.wireOp",EDGE,"E72.1");var subQ16=sQuery(id+"F12.wireOp",EDGE,"E74.1");var subQ18=sQuery(id+"F12.wireOp",EDGE,"E74.8");Q0=qUnion([makeQuery(id+"F12.imprint","IMPRINT",FACE,{"disambiguationData":[TD([[makeQuery(id+"F12.imprint","IMPRINT",EDGE,{"derivedFrom":subQ7}),1.0]])]}),makeQuery(id+"F12.imprint","IMPRINT",FACE,{"disambiguationData":[TD([[makeQuery(id+"F12.imprint","IMPRINT",EDGE,{"derivedFrom":subQ14}),1.0]])]}),makeQuery(id+"F12.imprint","IMPRINT",FACE,{"disambiguationData":[TD([[makeQuery(id+"F12.imprint","IMPRINT",EDGE,{"derivedFrom":subQ16}),1.0]])]}),makeQuery(id+"F12.imprint","IMPRINT",FACE,{"disambiguationData":[TD([[makeQuery(id+"F12.imprint","IMPRINT",EDGE,{"derivedFrom":subQ18}),-1.0]])]})]);}
            var Q1;
            Q1=makeQuery(id+"F5.boolean.opBoolean","SPLIT",FACE,{"disambiguationData":[TD([makeQuery(id+"F5.opExtrude","SWEPT_FACE",FACE,{"disambiguationData":[OSD([sQuery(id+"F4.wireOp",EDGE,"E41")])]})])],"derivedFrom":makeQuery(id+"F3.boolean.opBoolean","COPY",FACE,{"derivedFrom":makeQuery(id+"F3.opExtrude","CAP_FACE",FACE,{"disambiguationData":[OSD([sQuery(id+"F0.wireOp",EDGE,"E25.0"),sQuery(id+"F0.wireOp",EDGE,"E25.1"),sQuery(id+"F0.wireOp",EDGE,"E25.2"),sQuery(id+"F0.wireOp",EDGE,"E25.3"),sQuery(id+"F0.wireOp",EDGE,"E25.4"),sQuery(id+"F0.wireOp",EDGE,"E25.5"),sQuery(id+"F0.wireOp",EDGE,"E25.6"),sQuery(id+"F0.wireOp",EDGE,"E25.7")])],"isStart":false})})});
            extrude(context, id + "F13", {"entities" : qUnion([Q0]), "operationType" : NewBodyOperationType.REMOVE, "endBound" : BoundingType.UP_TO_SURFACE, "endBoundEntityFace" : qUnion([Q1]), "depth" : 25 * mm});
        }
        {
            var Q0;
            Q0=makeQuery(id+"F3.boolean.opBoolean","COPY",EDGE,{"derivedFrom":makeQuery(id+"F3.opExtrude","CAP_EDGE",EDGE,{"disambiguationData":[OSD([sQuery(id+"F0.wireOp",EDGE,"E25.6")])],"isStart":false})});
            var Q1;
            Q1=makeQuery(id+"F8.boolean.opBoolean","INTERSECT",EDGE,{"derivedFrom":[makeQuery(id+"F5.opExtrude","SWEPT_FACE",FACE,{"disambiguationData":[OSD([sQuery(id+"F4.wireOp",EDGE,"E30")])]}),makeQuery(id+"F8.opExtrude","CAP_FACE",FACE,{"disambiguationData":[OSD([sQuery(id+"F7.wireOp",EDGE,"E67")])],"isStart":false})]});
            var Q2;
            Q2=makeQuery(id+"F8.boolean.opBoolean","INTERSECT",EDGE,{"disambiguationData":[OD(1.0)],"derivedFrom":[makeQuery(id+"F5.opExtrude","SWEPT_FACE",FACE,{"disambiguationData":[OSD([sQuery(id+"F4.wireOp",EDGE,"E30")])]}),makeQuery(id+"F8.opExtrude","SWEPT_FACE",FACE,{"disambiguationData":[OSD([sQuery(id+"F7.wireOp",EDGE,"E67")])]})]});
            var Q3;
            {var subQ0=sQuery(id+"F4.wireOp",EDGE,"E30");Q3=makeQuery(id+"F8.boolean.opBoolean","SPLIT",EDGE,{"disambiguationData":[TD([makeQuery(id+"F5.opExtrude","SWEPT_FACE",FACE,{"disambiguationData":[OSD([sQuery(id+"F4.wireOp",EDGE,"E35.filletArc")])]})])],"derivedFrom":makeQuery(id+"F5.opExtrude","CAP_EDGE",EDGE,{"disambiguationData":[OSD([subQ0])],"isStart":false})});}
            var Q4;
            {var subQ0=sQuery(id+"F0.wireOp",EDGE,"E25.7");var subQ1=sQuery(id+"F0.wireOp",EDGE,"E25.1");var subQ2=sQuery(id+"F0.wireOp",EDGE,"E25.6");var subQ3=sQuery(id+"F0.wireOp",EDGE,"E25.5");var subQ4=sQuery(id+"F0.wireOp",EDGE,"E25.4");var subQ5=sQuery(id+"F0.wireOp",EDGE,"E25.0");var subQ6=sQuery(id+"F0.wireOp",EDGE,"E25.2");var subQ7=sQuery(id+"F0.wireOp",EDGE,"E25.3");Q4=makeQuery(id+"F8.boolean.opBoolean","INTERSECT",EDGE,{"derivedFrom":[makeQuery(id+"F5.boolean.opBoolean","SPLIT",FACE,{"disambiguationData":[TD([makeQuery(id+"F2.opExtrude","SWEPT_FACE",FACE,{"disambiguationData":[OSD([subQ5])]})])],"derivedFrom":makeQuery(id+"F3.boolean.opBoolean","COPY",FACE,{"derivedFrom":makeQuery(id+"F3.opExtrude","CAP_FACE",FACE,{"disambiguationData":[OSD([subQ5,subQ1,subQ6,subQ7,subQ4,subQ3,subQ2,subQ0])],"isStart":false})})}),makeQuery(id+"F8.opExtrude","SWEPT_FACE",FACE,{"disambiguationData":[OSD([sQuery(id+"F7.wireOp",EDGE,"E67")])]})]});}
            var Q5;
            Q5=makeQuery(id+"F8.boolean.opBoolean","INTERSECT",EDGE,{"disambiguationData":[OD(0.0)],"derivedFrom":[makeQuery(id+"F5.opExtrude","SWEPT_FACE",FACE,{"disambiguationData":[OSD([sQuery(id+"F4.wireOp",EDGE,"E30")])]}),makeQuery(id+"F8.opExtrude","SWEPT_FACE",FACE,{"disambiguationData":[OSD([sQuery(id+"F7.wireOp",EDGE,"E67")])]})]});
            fillet(context, id + "F14", {"entities" : qUnion([Q0, Q1, Q2, Q3, Q4, Q5]), "radius" : 3 * mm, "tangentPropagation" : true, "allowEdgeOverflow" : false});
        }
        {
            var Q0;
            Q0=makeQuery(id+"F1.opExtrude","CAP_EDGE",EDGE,{"disambiguationData":[OSD([sQuery(id+"F0.wireOp",EDGE,"E1.bottom")])],"isStart":false});
            fillet(context, id + "F15", {"entities" : qUnion([Q0]), "radius" : 2 * mm, "tangentPropagation" : true, "allowEdgeOverflow" : false});
        }
        {
            var Q0;
            {var subQ0=sQuery(id+"F0.wireOp",EDGE,"E21.filletArc");var subQ1=sQuery(id+"F0.wireOp",EDGE,"E7");var subQ2=sQuery(id+"F0.wireOp",EDGE,"E6");var subQ3=sQuery(id+"F0.wireOp",EDGE,"E5");var subQ4=sQuery(id+"F0.wireOp",EDGE,"E4");var subQ5=sQuery(id+"F0.wireOp",EDGE,"E22.filletArc");var subQ6=sQuery(id+"F0.wireOp",EDGE,"E1.bottom");var subQ7=sQuery(id+"F0.wireOp",EDGE,"E1.right");var subQ8=sQuery(id+"F0.wireOp",EDGE,"E1.top");var subQ9=sQuery(id+"F0.wireOp",EDGE,"E1.left");var subQ10=sQuery(id+"F0.wireOp",EDGE,"E23.filletArc");var subQ11=sQuery(id+"F0.wireOp",EDGE,"E24.filletArc");Q0=makeQuery(id+"F2.boolean.opBoolean","SPLIT",FACE,{"disambiguationData":[TD([makeQuery(id+"F1.opExtrude","SWEPT_FACE",FACE,{"disambiguationData":[OSD([subQ6])]})])],"derivedFrom":makeQuery(id+"F1.opExtrude","CAP_FACE",FACE,{"disambiguationData":[OSD([subQ6,subQ8,subQ9,subQ7,subQ4,subQ3,subQ2,subQ1,subQ0,subQ5,subQ10,subQ11])],"isStart":true})});}
            var sketch = newSketch(context, id + "F16", { "sketchPlane" : qUnion([Q0])});
            skLineSegment(sketch, "E79.0", {"start": v(-70, 90) * mm, "end": v(70, 90) * mm});
            skArc(sketch, "E79.1", {"start": v(-70, 90) * mm, "mid": v(-77.07, 87.07) * mm, "end": v(-80, 80) * mm});
            skLineSegment(sketch, "E79.2", {"start": v(-80, -80) * mm, "end": v(-80, 80) * mm});
            skCircle(sketch, "E79.3", {"center": v(-60, 67.5) * mm, "radius": 4 * mm});
            skLineSegment(sketch, "E79.4", {"start": v(-60, 40.3) * mm, "end": v(-60, -40.3) * mm});
            skArc(sketch, "E79.5", {"start": v(-56.15, 48.18) * mm, "mid": v(-58.99, 44.68) * mm, "end": v(-60, 40.3) * mm});
            skArc(sketch, "E79.6", {"start": v(56.15, 48.18) * mm, "mid": v(0, 67.5) * mm, "end": v(-56.15, 48.18) * mm});
            skLineSegment(sketch, "E79.7", {"start": v(60, 40.3) * mm, "end": v(60, -40.3) * mm});
            skArc(sketch, "E79.8", {"start": v(60, 40.3) * mm, "mid": v(58.99, 44.68) * mm, "end": v(56.15, 48.18) * mm});
            skArc(sketch, "E79.9", {"start": v(56.15, -48.18) * mm, "mid": v(58.99, -44.68) * mm, "end": v(60, -40.3) * mm});
            skArc(sketch, "E79.10", {"start": v(-56.15, -48.18) * mm, "mid": v(0, -67.5) * mm, "end": v(56.15, -48.18) * mm});
            skArc(sketch, "E79.11", {"start": v(-60, -40.3) * mm, "mid": v(-58.99, -44.68) * mm, "end": v(-56.15, -48.18) * mm});
            skLineSegment(sketch, "E79.12", {"start": v(80, -80) * mm, "end": v(80, 80) * mm});
            skArc(sketch, "E79.13", {"start": v(80, 80) * mm, "mid": v(77.07, 87.07) * mm, "end": v(70, 90) * mm});
            skCircle(sketch, "E79.14", {"center": v(60, -67.5) * mm, "radius": 4 * mm});
            skCircle(sketch, "E79.15", {"center": v(60, 67.5) * mm, "radius": 4 * mm});
            skCircle(sketch, "E79.16", {"center": v(-60, -67.5) * mm, "radius": 4 * mm});
            skLineSegment(sketch, "E79.17", {"start": v(-70, -90) * mm, "end": v(70, -90) * mm});
            skArc(sketch, "E79.18", {"start": v(-80, -80) * mm, "mid": v(-77.07, -87.07) * mm, "end": v(-70, -90) * mm});
            skArc(sketch, "E79.19", {"start": v(70, -90) * mm, "mid": v(77.07, -87.07) * mm, "end": v(80, -80) * mm});
            skPoint(sketch, "E80.centerSnap0", {"position": v(0, 90) * mm});
            skLineSegment(sketch, "E81", {"start": v(0, 90) * mm, "end": v(0, 120) * mm, "construction": true});
            skCircle(sketch, "E82", {"center": v(0, 120) * mm, "radius": 6 * mm});
            skLineSegment(sketch, "E83", {"start": v(-33, 90) * mm, "end": v(-15, 108) * mm});
            skLineSegment(sketch, "E84", {"start": v(-15, 108) * mm, "end": v(-15, 120) * mm});
            skArc(sketch, "E85", {"start": v(15, 120) * mm, "mid": v(0, 135) * mm, "end": v(-15, 120) * mm});
            skLineSegment(sketch, "E86", {"start": v(15, 120) * mm, "end": v(15, 108) * mm});
            skLineSegment(sketch, "E87", {"start": v(15, 108) * mm, "end": v(33, 90) * mm});
            skLineSegment(sketch, "E88", {"start": v(-80, 0) * mm, "end": v(80, 0) * mm, "construction": true});
            skArc(sketch, "E89.MirrorCS", {"start": v(15, -120) * mm, "mid": v(0, -135) * mm, "end": v(-15, -120) * mm});
            skLineSegment(sketch, "E90.MirrorCS", {"start": v(15, -120) * mm, "end": v(15, -108) * mm});
            skLineSegment(sketch, "E91.MirrorCS", {"start": v(15, -108) * mm, "end": v(33, -90) * mm});
            skLineSegment(sketch, "E92.MirrorCS", {"start": v(-15, -108) * mm, "end": v(-15, -120) * mm});
            skLineSegment(sketch, "E93.MirrorCS", {"start": v(-33, -90) * mm, "end": v(-15, -108) * mm});
            skLineSegment(sketch, "E94.MirrorCS", {"start": v(0, -90) * mm, "end": v(0, -120) * mm, "construction": true});
            skCircle(sketch, "E95.MirrorC", {"center": v(0, -120) * mm, "radius": 6 * mm});
            skSolve(sketch);
        }
        {
            var Q0;
            Q0 = qSketchRegion(id + "F16", true);
            var Q1;
            Q1=makeQuery(id+"F2.opExtrude","CAP_FACE",FACE,{"disambiguationData":[OSD([sQuery(id+"F0.wireOp",EDGE,"E12"),sQuery(id+"F0.wireOp",EDGE,"E13"),sQuery(id+"F0.wireOp",EDGE,"E14"),sQuery(id+"F0.wireOp",EDGE,"E15"),sQuery(id+"F0.wireOp",EDGE,"E17.filletArc"),sQuery(id+"F0.wireOp",EDGE,"E18.filletArc"),sQuery(id+"F0.wireOp",EDGE,"E19.filletArc"),sQuery(id+"F0.wireOp",EDGE,"E20.filletArc"),sQuery(id+"F0.wireOp",EDGE,"E25.0"),sQuery(id+"F0.wireOp",EDGE,"E25.1"),sQuery(id+"F0.wireOp",EDGE,"E25.2"),sQuery(id+"F0.wireOp",EDGE,"E25.3"),sQuery(id+"F0.wireOp",EDGE,"E25.4"),sQuery(id+"F0.wireOp",EDGE,"E25.5"),sQuery(id+"F0.wireOp",EDGE,"E25.6"),sQuery(id+"F0.wireOp",EDGE,"E25.7")])],"isStart":false});
            extrude(context, id + "F17", {"entities" : qUnion([Q0]), "endBound" : BoundingType.UP_TO_SURFACE, "depth" : 25 * mm, "endBoundEntityFace" : qUnion([Q1]), "offsetDistance" : 25 * mm});
        }
    });
